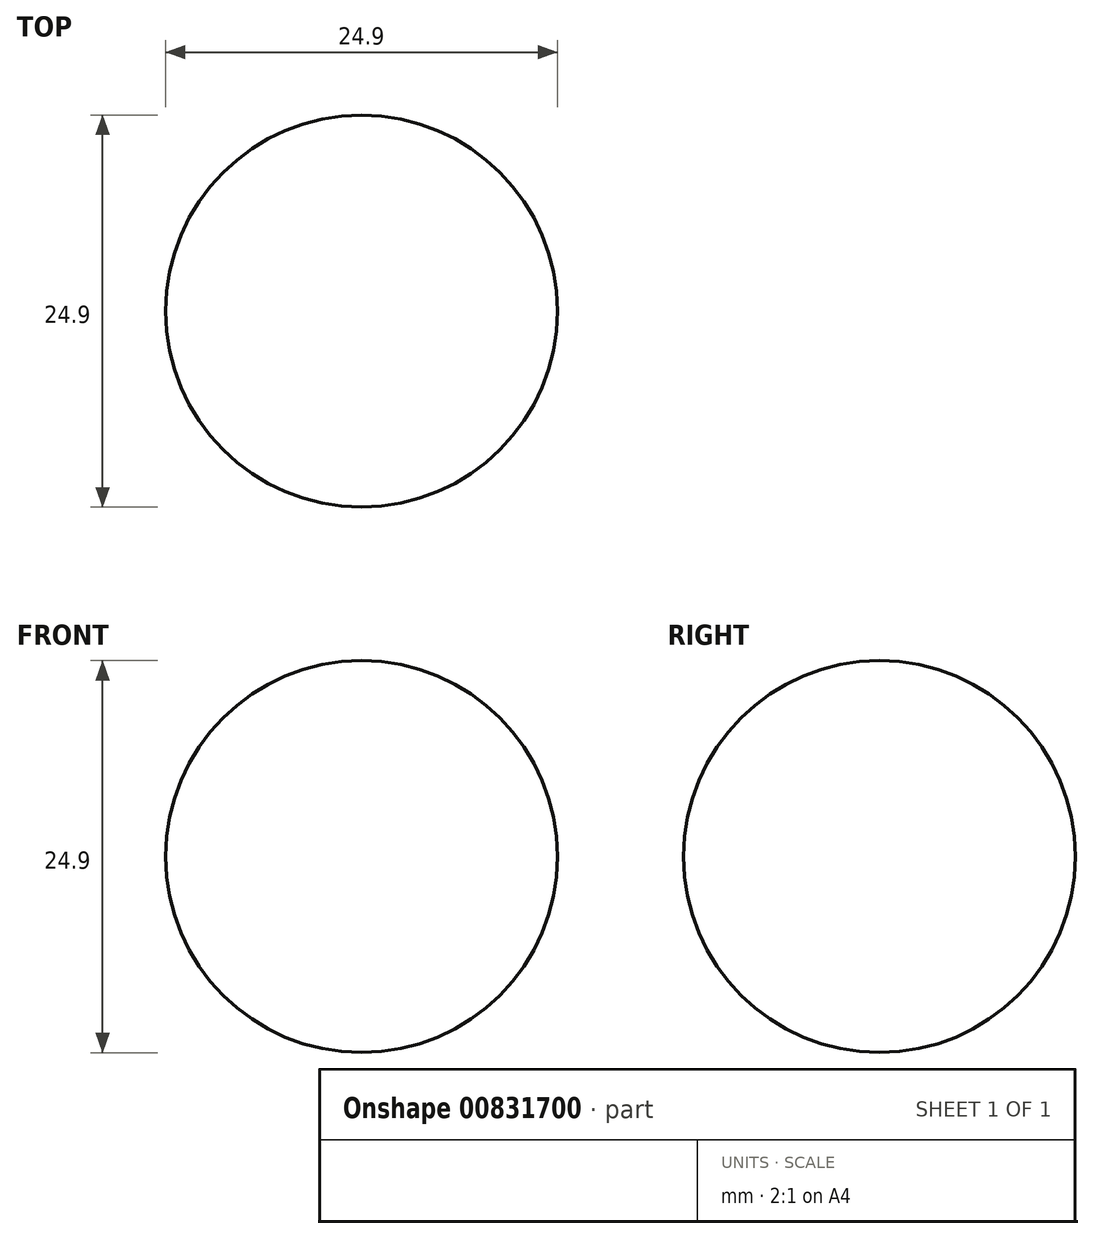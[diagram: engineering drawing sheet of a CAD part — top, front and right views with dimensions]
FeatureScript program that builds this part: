
annotation { "Feature Type Name" : "Feature", "Feature Type Description" : "" }
export const myFeature = defineFeature(function(context is Context, id is Id, definition is map)
    precondition{}
    {
        {
            var Q0;
            Q0=qCreatedBy(makeId("Front.planeOp"),FACE);
            var sketch = newSketch(context, id + "F0", { "sketchPlane" : qUnion([Q0])});
            skArc(sketch, "E0", {"start": v(0, -12.45) * mm, "mid": v(12.45, 0) * mm, "end": v(0, 12.45) * mm});
            skLineSegment(sketch, "E1", {"start": v(0, 12.45) * mm, "end": v(0, -12.45) * mm});
            skPoint(sketch, "E2.orphan", {"position": v(0, 15.41) * mm});
            skPoint(sketch, "E3.start.orphan", {"position": v(12.45, 0) * mm});
            skSolve(sketch);
        }
        {
            var Q0;
            Q0=makeQuery(id+"F0.imprint","IMPRINT",FACE,{"disambiguationData":[TD([[makeQuery(id+"F0.imprint","IMPRINT",EDGE,{"derivedFrom":sQuery(id+"F0.wireOp",EDGE,"E0")}),1.0]])]});
            var Q1;
            Q1=sQuery(id+"F0.wireOp",EDGE,"E1");
            revolve(context, id + "F1", {"surfaceOperationType" : NewSurfaceOperationType.NEW, "entities" : qUnion([Q0]), "axis" : qUnion([Q1]), "revolveType" : RevolveType.FULL});
        }
    });
